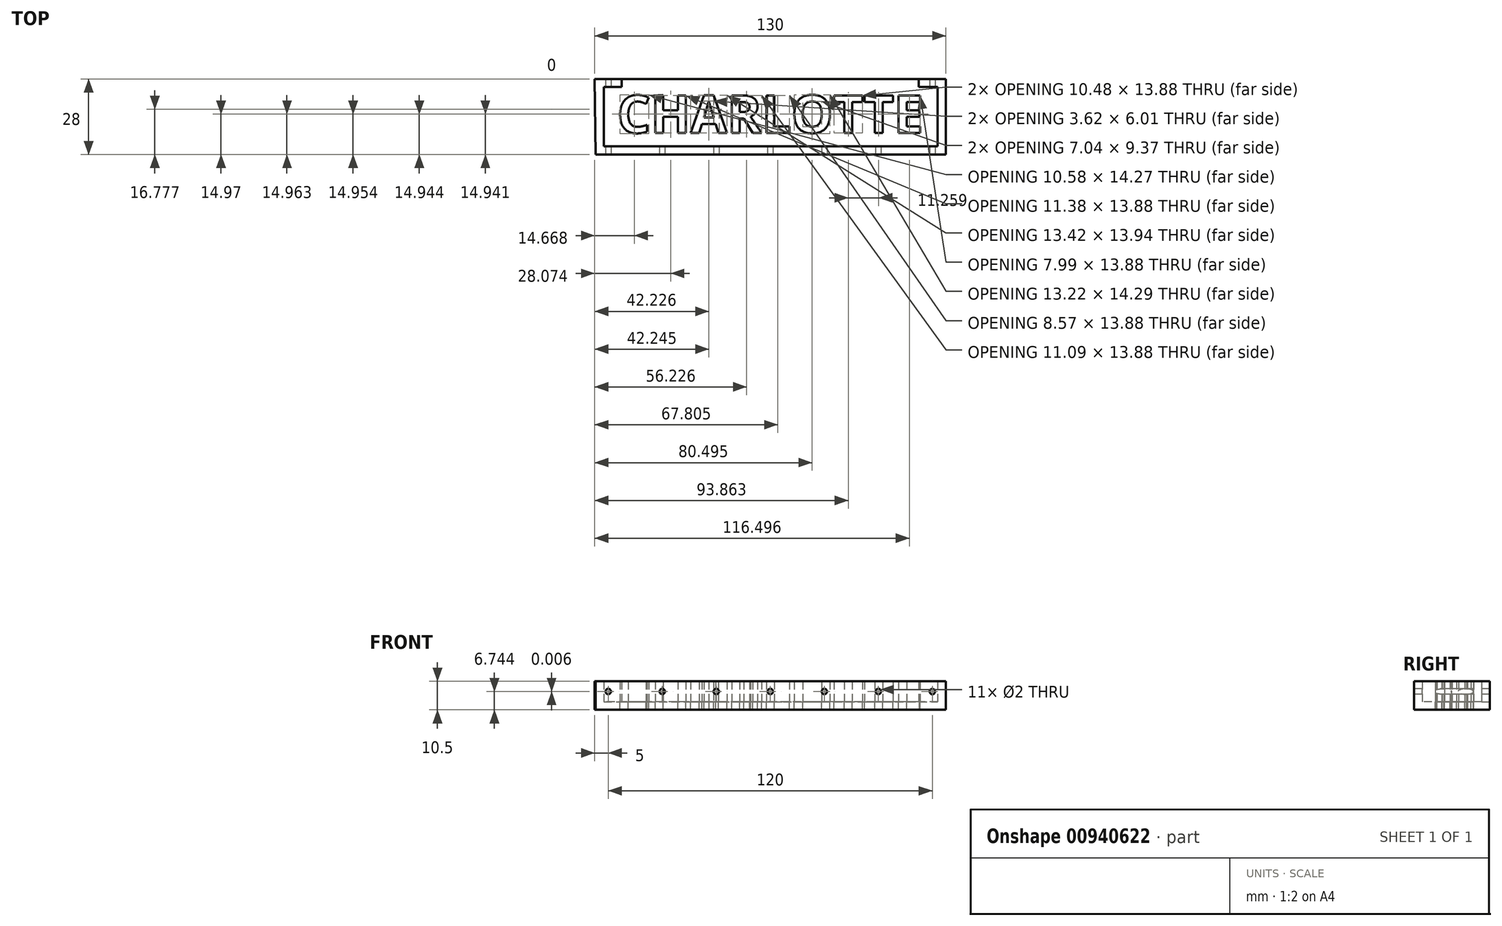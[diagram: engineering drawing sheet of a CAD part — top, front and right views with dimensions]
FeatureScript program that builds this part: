
annotation { "Feature Type Name" : "Feature", "Feature Type Description" : "" }
export const myFeature = defineFeature(function(context is Context, id is Id, definition is map)
    precondition{}
    {
        {
            var Q0;
            Q0=qCreatedBy(makeId("Top.planeOp"),FACE);
            var sketch = newSketch(context, id + "F0", { "sketchPlane" : qUnion([Q0])});
            skText(sketch, "E0", { "text": "CHARLOTTE", "fontName": "OpenSans-Bold.ttf"});
            skLineSegment(sketch, "E1", {"start": v(62, 11) * mm, "end": v(62, -11) * mm});
            skLineSegment(sketch, "E2", {"start": v(62, -11) * mm, "end": v(-61.65, -11) * mm});
            skLineSegment(sketch, "E3", {"start": v(-61.65, -11) * mm, "end": v(-61.65, 11) * mm});
            skLineSegment(sketch, "E4", {"start": v(-65, 14) * mm, "end": v(65, 14) * mm});
            skLineSegment(sketch, "E5", {"start": v(65, 14) * mm, "end": v(65, -14) * mm});
            skLineSegment(sketch, "E6", {"start": v(65, -14) * mm, "end": v(-64.65, -14) * mm});
            skLineSegment(sketch, "E7", {"start": v(-64.65, -14) * mm, "end": v(-65, 14) * mm});
            skPoint(sketch, "E8", {"position": v(0, 14) * mm});
            skPoint(sketch, "E9", {"position": v(-64.83, 0) * mm});
            skPoint(sketch, "E9.positionSnap0", {"position": v(-64.83, 0) * mm});
            skPoint(sketch, "E10", {"position": v(-56.75, 1) * mm});
            skPoint(sketch, "E11", {"position": v(-55, 14) * mm});
            skPoint(sketch, "E12", {"position": v(-55, 11) * mm});
            skPoint(sketch, "E13", {"position": v(55, 14) * mm});
            skPoint(sketch, "E14", {"position": v(55, 11) * mm});
            skLineSegment(sketch, "E15", {"start": v(-55, 11) * mm, "end": v(-55, 14) * mm});
            skLineSegment(sketch, "E16", {"start": v(55, 11) * mm, "end": v(55, 14) * mm});
            skLineSegment(sketch, "E17", {"start": v(-61.65, 11) * mm, "end": v(-55, 11) * mm});
            skLineSegment(sketch, "E18", {"start": v(55, 11) * mm, "end": v(62, 11) * mm});
            const initialGuessF0  = {"E0": [-0.05675, -0.006, 1, 0, 0.014]};
            skSetInitialGuess(sketch, initialGuessF0);
            skSolve(sketch);
        }
        {
            var Q0;
            Q0=makeQuery(id+"F0.imprint","IMPRINT",FACE,{"disambiguationData":[TD([[makeQuery(id+"F0.imprint","IMPRINT",EDGE,{"derivedFrom":sQuery(id+"F0.wireOp",EDGE,"E1")}),1.0]])]});
            var Q1;
            Q1=makeQuery(id+"F0.imprint","IMPRINT",FACE,{"disambiguationData":[TD([[makeQuery(id+"F0.imprint","IMPRINT",EDGE,{"derivedFrom":sQuery(id+"F0.wireOp",EDGE,"E0.sketch_text.stroke-15")}),-1.0]])]});
            var Q2;
            Q2=makeQuery(id+"F0.imprint","IMPRINT",FACE,{"disambiguationData":[TD([[makeQuery(id+"F0.imprint","IMPRINT",EDGE,{"derivedFrom":sQuery(id+"F0.wireOp",EDGE,"E0.sketch_text.stroke-64")}),-1.0]])]});
            var Q3;
            Q3=makeQuery(id+"F0.imprint","IMPRINT",FACE,{"disambiguationData":[TD([[makeQuery(id+"F0.imprint","IMPRINT",EDGE,{"derivedFrom":sQuery(id+"F0.wireOp",EDGE,"E0.sketch_text.stroke-58")}),-1.0]])]});
            var Q4;
            Q4=makeQuery(id+"F0.imprint","IMPRINT",FACE,{"disambiguationData":[TD([[makeQuery(id+"F0.imprint","IMPRINT",EDGE,{"derivedFrom":sQuery(id+"F0.wireOp",EDGE,"E0.sketch_text.stroke-39")}),-1.0]])]});
            var Q5;
            Q5=makeQuery(id+"F0.imprint","IMPRINT",FACE,{"disambiguationData":[TD([[makeQuery(id+"F0.imprint","IMPRINT",EDGE,{"derivedFrom":sQuery(id+"F0.wireOp",EDGE,"E0.sketch_text.stroke-27")}),-1.0]])]});
            var Q6;
            Q6=makeQuery(id+"F0.imprint","IMPRINT",FACE,{"disambiguationData":[TD([[makeQuery(id+"F0.imprint","IMPRINT",EDGE,{"derivedFrom":sQuery(id+"F0.wireOp",EDGE,"E0.sketch_text.stroke-78")}),-1.0]])]});
            var Q7;
            Q7=makeQuery(id+"F0.imprint","IMPRINT",FACE,{"disambiguationData":[TD([[makeQuery(id+"F0.imprint","IMPRINT",EDGE,{"derivedFrom":sQuery(id+"F0.wireOp",EDGE,"E0.sketch_text.stroke-86")}),-1.0]])]});
            var Q8;
            Q8=makeQuery(id+"F0.imprint","IMPRINT",FACE,{"disambiguationData":[TD([[makeQuery(id+"F0.imprint","IMPRINT",EDGE,{"derivedFrom":sQuery(id+"F0.wireOp",EDGE,"E0.sketch_text.stroke-94")}),-1.0]])]});
            var Q9;
            Q9=makeQuery(id+"F0.imprint","IMPRINT",FACE,{"disambiguationData":[TD([[makeQuery(id+"F0.imprint","IMPRINT",EDGE,{"derivedFrom":sQuery(id+"F0.wireOp",EDGE,"E0.sketch_text.stroke-0")}),-1.0]])]});
            extrude(context, id + "F1", {"entities" : qUnion([Q0, Q1, Q2, Q3, Q4, Q5, Q6, Q7, Q8, Q9]), "depth" : 7.5 * mm});
        }
        {
            var Q0;
            Q0=qSketchRegion(id+"F0",true);
            extrude(context, id + "F2", {"entities" : qUnion([Q0]), "operationType" : NewBodyOperationType.ADD, "depth" : -3 * mm});
        }
        {
            var Q0;
            {var subQ0=sQuery(id+"F0.wireOp",EDGE,"E6");Q0=makeQuery(id+"F2.boolean.opBoolean","MERGE",FACE,{"derivedFrom":[makeQuery(id+"F1.opExtrude","SWEPT_FACE",FACE,{"disambiguationData":[OSD([subQ0])]}),makeQuery(id+"F2.opExtrude","SWEPT_FACE",FACE,{"disambiguationData":[OSD([subQ0])]})]});}
            var sketch = newSketch(context, id + "F3", { "sketchPlane" : qUnion([Q0])});
            skPoint(sketch, "E19", {"position": v(-60, 3.75) * mm});
            skPoint(sketch, "E20", {"position": v(60, 3.74) * mm});
            skPoint(sketch, "E21", {"position": v(-40, 3.75) * mm});
            skPoint(sketch, "E22", {"position": v(-20, 3.75) * mm});
            skPoint(sketch, "E23", {"position": v(0, 3.75) * mm});
            skPoint(sketch, "E24", {"position": v(20, 3.75) * mm});
            skPoint(sketch, "E25", {"position": v(40, 3.75) * mm});
            skSolve(sketch);
        }
        {
            var Q0;
            Q0=sQuery(id+"F3.wireOp",VERTEX,"E19");
            var Q1;
            Q1=sQuery(id+"F3.wireOp",VERTEX,"E21");
            var Q2;
            Q2=sQuery(id+"F3.wireOp",VERTEX,"E22");
            var Q3;
            Q3=sQuery(id+"F3.wireOp",VERTEX,"E23");
            var Q4;
            Q4=sQuery(id+"F3.wireOp",VERTEX,"E24");
            var Q5;
            Q5=sQuery(id+"F3.wireOp",VERTEX,"E25");
            var Q6;
            Q6=sQuery(id+"F3.wireOp",VERTEX,"E20");
            var Q7;
            Q7=makeQuery(id+"F1.opExtrude","SWEPT_BODY",BODY,{"disambiguationData":[OSD([sQuery(id+"F0.wireOp",EDGE,"E1"),sQuery(id+"F0.wireOp",EDGE,"E2"),sQuery(id+"F0.wireOp",EDGE,"E3"),sQuery(id+"F0.wireOp",EDGE,"E4"),sQuery(id+"F0.wireOp",EDGE,"E5"),sQuery(id+"F0.wireOp",EDGE,"E6"),sQuery(id+"F0.wireOp",EDGE,"E7"),sQuery(id+"F0.wireOp",EDGE,"E15"),sQuery(id+"F0.wireOp",EDGE,"E16"),sQuery(id+"F0.wireOp",EDGE,"E17"),sQuery(id+"F0.wireOp",EDGE,"E18")])]});
            var Q8;
            Q8=makeQuery(id+"F1.opExtrude","SWEPT_BODY",BODY,{"disambiguationData":[OSD([sQuery(id+"F0.wireOp",EDGE,"E0.sketch_text.stroke-0"),sQuery(id+"F0.wireOp",EDGE,"E0.sketch_text.stroke-1"),sQuery(id+"F0.wireOp",EDGE,"E0.sketch_text.stroke-2"),sQuery(id+"F0.wireOp",EDGE,"E0.sketch_text.stroke-3"),sQuery(id+"F0.wireOp",EDGE,"E0.sketch_text.stroke-4"),sQuery(id+"F0.wireOp",EDGE,"E0.sketch_text.stroke-5"),sQuery(id+"F0.wireOp",EDGE,"E0.sketch_text.stroke-6"),sQuery(id+"F0.wireOp",EDGE,"E0.sketch_text.stroke-7"),sQuery(id+"F0.wireOp",EDGE,"E0.sketch_text.stroke-8"),sQuery(id+"F0.wireOp",EDGE,"E0.sketch_text.stroke-9"),sQuery(id+"F0.wireOp",EDGE,"E0.sketch_text.stroke-10"),sQuery(id+"F0.wireOp",EDGE,"E0.sketch_text.stroke-11"),sQuery(id+"F0.wireOp",EDGE,"E0.sketch_text.stroke-12"),sQuery(id+"F0.wireOp",EDGE,"E0.sketch_text.stroke-13"),sQuery(id+"F0.wireOp",EDGE,"E0.sketch_text.stroke-14")])]});
            var Q9;
            Q9=makeQuery(id+"F1.opExtrude","SWEPT_BODY",BODY,{"disambiguationData":[OSD([sQuery(id+"F0.wireOp",EDGE,"E0.sketch_text.stroke-27"),sQuery(id+"F0.wireOp",EDGE,"E0.sketch_text.stroke-28"),sQuery(id+"F0.wireOp",EDGE,"E0.sketch_text.stroke-29"),sQuery(id+"F0.wireOp",EDGE,"E0.sketch_text.stroke-30"),sQuery(id+"F0.wireOp",EDGE,"E0.sketch_text.stroke-31"),sQuery(id+"F0.wireOp",EDGE,"E0.sketch_text.stroke-32"),sQuery(id+"F0.wireOp",EDGE,"E0.sketch_text.stroke-33"),sQuery(id+"F0.wireOp",EDGE,"E0.sketch_text.stroke-34"),sQuery(id+"F0.wireOp",EDGE,"E0.sketch_text.stroke-35"),sQuery(id+"F0.wireOp",EDGE,"E0.sketch_text.stroke-36"),sQuery(id+"F0.wireOp",EDGE,"E0.sketch_text.stroke-37"),sQuery(id+"F0.wireOp",EDGE,"E0.sketch_text.stroke-38")])]});
            var Q10;
            Q10=makeQuery(id+"F1.opExtrude","SWEPT_BODY",BODY,{"disambiguationData":[OSD([sQuery(id+"F0.wireOp",EDGE,"E0.sketch_text.stroke-58"),sQuery(id+"F0.wireOp",EDGE,"E0.sketch_text.stroke-59"),sQuery(id+"F0.wireOp",EDGE,"E0.sketch_text.stroke-60"),sQuery(id+"F0.wireOp",EDGE,"E0.sketch_text.stroke-61"),sQuery(id+"F0.wireOp",EDGE,"E0.sketch_text.stroke-62"),sQuery(id+"F0.wireOp",EDGE,"E0.sketch_text.stroke-63")])]});
            var Q11;
            Q11=makeQuery(id+"F1.opExtrude","SWEPT_BODY",BODY,{"disambiguationData":[OSD([sQuery(id+"F0.wireOp",EDGE,"E0.sketch_text.stroke-78"),sQuery(id+"F0.wireOp",EDGE,"E0.sketch_text.stroke-79"),sQuery(id+"F0.wireOp",EDGE,"E0.sketch_text.stroke-80"),sQuery(id+"F0.wireOp",EDGE,"E0.sketch_text.stroke-81"),sQuery(id+"F0.wireOp",EDGE,"E0.sketch_text.stroke-82"),sQuery(id+"F0.wireOp",EDGE,"E0.sketch_text.stroke-83"),sQuery(id+"F0.wireOp",EDGE,"E0.sketch_text.stroke-84"),sQuery(id+"F0.wireOp",EDGE,"E0.sketch_text.stroke-85")])]});
            var Q12;
            Q12=makeQuery(id+"F1.opExtrude","SWEPT_BODY",BODY,{"disambiguationData":[OSD([sQuery(id+"F0.wireOp",EDGE,"E0.sketch_text.stroke-94"),sQuery(id+"F0.wireOp",EDGE,"E0.sketch_text.stroke-95"),sQuery(id+"F0.wireOp",EDGE,"E0.sketch_text.stroke-96"),sQuery(id+"F0.wireOp",EDGE,"E0.sketch_text.stroke-97"),sQuery(id+"F0.wireOp",EDGE,"E0.sketch_text.stroke-98"),sQuery(id+"F0.wireOp",EDGE,"E0.sketch_text.stroke-99"),sQuery(id+"F0.wireOp",EDGE,"E0.sketch_text.stroke-100"),sQuery(id+"F0.wireOp",EDGE,"E0.sketch_text.stroke-101"),sQuery(id+"F0.wireOp",EDGE,"E0.sketch_text.stroke-102"),sQuery(id+"F0.wireOp",EDGE,"E0.sketch_text.stroke-103"),sQuery(id+"F0.wireOp",EDGE,"E0.sketch_text.stroke-104"),sQuery(id+"F0.wireOp",EDGE,"E0.sketch_text.stroke-105")])]});
            hole(context, id + "F4", {"style" : HoleStyle.SIMPLE, "endStyle" : HoleEndStyle.THROUGH, "holeDiameter" : 2 * mm, "isTappedThrough" : true, "tappedDepth" : 12.7 * mm, "tapClearance" : 3, "locations" : qUnion([Q0, Q1, Q2, Q3, Q4, Q5, Q6]), "scope" : qUnion([Q7, Q8, Q9, Q10, Q11, Q12])});
        }
        {
            var Q0;
            Q0=makeQuery(id+"F1.opExtrude","CAP_FACE",FACE,{"disambiguationData":[OSD([sQuery(id+"F0.wireOp",EDGE,"E0.sketch_text.stroke-0"),sQuery(id+"F0.wireOp",EDGE,"E0.sketch_text.stroke-1"),sQuery(id+"F0.wireOp",EDGE,"E0.sketch_text.stroke-2"),sQuery(id+"F0.wireOp",EDGE,"E0.sketch_text.stroke-3"),sQuery(id+"F0.wireOp",EDGE,"E0.sketch_text.stroke-4"),sQuery(id+"F0.wireOp",EDGE,"E0.sketch_text.stroke-5"),sQuery(id+"F0.wireOp",EDGE,"E0.sketch_text.stroke-6"),sQuery(id+"F0.wireOp",EDGE,"E0.sketch_text.stroke-7"),sQuery(id+"F0.wireOp",EDGE,"E0.sketch_text.stroke-8"),sQuery(id+"F0.wireOp",EDGE,"E0.sketch_text.stroke-9"),sQuery(id+"F0.wireOp",EDGE,"E0.sketch_text.stroke-10"),sQuery(id+"F0.wireOp",EDGE,"E0.sketch_text.stroke-11"),sQuery(id+"F0.wireOp",EDGE,"E0.sketch_text.stroke-12"),sQuery(id+"F0.wireOp",EDGE,"E0.sketch_text.stroke-13"),sQuery(id+"F0.wireOp",EDGE,"E0.sketch_text.stroke-14")])],"isStart":true});
            var Q1;
            Q1=makeQuery(id+"F1.opExtrude","CAP_FACE",FACE,{"disambiguationData":[OSD([sQuery(id+"F0.wireOp",EDGE,"E0.sketch_text.stroke-15"),sQuery(id+"F0.wireOp",EDGE,"E0.sketch_text.stroke-16"),sQuery(id+"F0.wireOp",EDGE,"E0.sketch_text.stroke-17"),sQuery(id+"F0.wireOp",EDGE,"E0.sketch_text.stroke-18"),sQuery(id+"F0.wireOp",EDGE,"E0.sketch_text.stroke-19"),sQuery(id+"F0.wireOp",EDGE,"E0.sketch_text.stroke-20"),sQuery(id+"F0.wireOp",EDGE,"E0.sketch_text.stroke-21"),sQuery(id+"F0.wireOp",EDGE,"E0.sketch_text.stroke-22"),sQuery(id+"F0.wireOp",EDGE,"E0.sketch_text.stroke-23"),sQuery(id+"F0.wireOp",EDGE,"E0.sketch_text.stroke-24"),sQuery(id+"F0.wireOp",EDGE,"E0.sketch_text.stroke-25"),sQuery(id+"F0.wireOp",EDGE,"E0.sketch_text.stroke-26")])],"isStart":true});
            var Q2;
            Q2=makeQuery(id+"F1.opExtrude","CAP_FACE",FACE,{"disambiguationData":[OSD([sQuery(id+"F0.wireOp",EDGE,"E0.sketch_text.stroke-27"),sQuery(id+"F0.wireOp",EDGE,"E0.sketch_text.stroke-28"),sQuery(id+"F0.wireOp",EDGE,"E0.sketch_text.stroke-29"),sQuery(id+"F0.wireOp",EDGE,"E0.sketch_text.stroke-30"),sQuery(id+"F0.wireOp",EDGE,"E0.sketch_text.stroke-31"),sQuery(id+"F0.wireOp",EDGE,"E0.sketch_text.stroke-32"),sQuery(id+"F0.wireOp",EDGE,"E0.sketch_text.stroke-33"),sQuery(id+"F0.wireOp",EDGE,"E0.sketch_text.stroke-34"),sQuery(id+"F0.wireOp",EDGE,"E0.sketch_text.stroke-35"),sQuery(id+"F0.wireOp",EDGE,"E0.sketch_text.stroke-36"),sQuery(id+"F0.wireOp",EDGE,"E0.sketch_text.stroke-37"),sQuery(id+"F0.wireOp",EDGE,"E0.sketch_text.stroke-38")])],"isStart":true});
            var Q3;
            Q3=makeQuery(id+"F1.opExtrude","CAP_FACE",FACE,{"disambiguationData":[OSD([sQuery(id+"F0.wireOp",EDGE,"E0.sketch_text.stroke-39"),sQuery(id+"F0.wireOp",EDGE,"E0.sketch_text.stroke-40"),sQuery(id+"F0.wireOp",EDGE,"E0.sketch_text.stroke-41"),sQuery(id+"F0.wireOp",EDGE,"E0.sketch_text.stroke-42"),sQuery(id+"F0.wireOp",EDGE,"E0.sketch_text.stroke-43"),sQuery(id+"F0.wireOp",EDGE,"E0.sketch_text.stroke-44"),sQuery(id+"F0.wireOp",EDGE,"E0.sketch_text.stroke-45"),sQuery(id+"F0.wireOp",EDGE,"E0.sketch_text.stroke-46"),sQuery(id+"F0.wireOp",EDGE,"E0.sketch_text.stroke-47"),sQuery(id+"F0.wireOp",EDGE,"E0.sketch_text.stroke-48"),sQuery(id+"F0.wireOp",EDGE,"E0.sketch_text.stroke-49"),sQuery(id+"F0.wireOp",EDGE,"E0.sketch_text.stroke-50"),sQuery(id+"F0.wireOp",EDGE,"E0.sketch_text.stroke-51"),sQuery(id+"F0.wireOp",EDGE,"E0.sketch_text.stroke-52"),sQuery(id+"F0.wireOp",EDGE,"E0.sketch_text.stroke-53"),sQuery(id+"F0.wireOp",EDGE,"E0.sketch_text.stroke-54"),sQuery(id+"F0.wireOp",EDGE,"E0.sketch_text.stroke-55"),sQuery(id+"F0.wireOp",EDGE,"E0.sketch_text.stroke-56"),sQuery(id+"F0.wireOp",EDGE,"E0.sketch_text.stroke-57")])],"isStart":true});
            var Q4;
            Q4=makeQuery(id+"F1.opExtrude","CAP_FACE",FACE,{"disambiguationData":[OSD([sQuery(id+"F0.wireOp",EDGE,"E0.sketch_text.stroke-58"),sQuery(id+"F0.wireOp",EDGE,"E0.sketch_text.stroke-59"),sQuery(id+"F0.wireOp",EDGE,"E0.sketch_text.stroke-60"),sQuery(id+"F0.wireOp",EDGE,"E0.sketch_text.stroke-61"),sQuery(id+"F0.wireOp",EDGE,"E0.sketch_text.stroke-62"),sQuery(id+"F0.wireOp",EDGE,"E0.sketch_text.stroke-63")])],"isStart":true});
            var Q5;
            Q5=makeQuery(id+"F1.opExtrude","CAP_FACE",FACE,{"disambiguationData":[OSD([sQuery(id+"F0.wireOp",EDGE,"E0.sketch_text.stroke-64"),sQuery(id+"F0.wireOp",EDGE,"E0.sketch_text.stroke-65"),sQuery(id+"F0.wireOp",EDGE,"E0.sketch_text.stroke-66"),sQuery(id+"F0.wireOp",EDGE,"E0.sketch_text.stroke-67"),sQuery(id+"F0.wireOp",EDGE,"E0.sketch_text.stroke-68"),sQuery(id+"F0.wireOp",EDGE,"E0.sketch_text.stroke-69"),sQuery(id+"F0.wireOp",EDGE,"E0.sketch_text.stroke-70"),sQuery(id+"F0.wireOp",EDGE,"E0.sketch_text.stroke-71"),sQuery(id+"F0.wireOp",EDGE,"E0.sketch_text.stroke-72"),sQuery(id+"F0.wireOp",EDGE,"E0.sketch_text.stroke-73"),sQuery(id+"F0.wireOp",EDGE,"E0.sketch_text.stroke-74"),sQuery(id+"F0.wireOp",EDGE,"E0.sketch_text.stroke-75"),sQuery(id+"F0.wireOp",EDGE,"E0.sketch_text.stroke-76"),sQuery(id+"F0.wireOp",EDGE,"E0.sketch_text.stroke-77")])],"isStart":true});
            var Q6;
            Q6=makeQuery(id+"F1.opExtrude","CAP_FACE",FACE,{"disambiguationData":[OSD([sQuery(id+"F0.wireOp",EDGE,"E0.sketch_text.stroke-78"),sQuery(id+"F0.wireOp",EDGE,"E0.sketch_text.stroke-79"),sQuery(id+"F0.wireOp",EDGE,"E0.sketch_text.stroke-80"),sQuery(id+"F0.wireOp",EDGE,"E0.sketch_text.stroke-81"),sQuery(id+"F0.wireOp",EDGE,"E0.sketch_text.stroke-82"),sQuery(id+"F0.wireOp",EDGE,"E0.sketch_text.stroke-83"),sQuery(id+"F0.wireOp",EDGE,"E0.sketch_text.stroke-84"),sQuery(id+"F0.wireOp",EDGE,"E0.sketch_text.stroke-85")])],"isStart":true});
            var Q7;
            Q7=makeQuery(id+"F1.opExtrude","CAP_FACE",FACE,{"disambiguationData":[OSD([sQuery(id+"F0.wireOp",EDGE,"E0.sketch_text.stroke-86"),sQuery(id+"F0.wireOp",EDGE,"E0.sketch_text.stroke-87"),sQuery(id+"F0.wireOp",EDGE,"E0.sketch_text.stroke-88"),sQuery(id+"F0.wireOp",EDGE,"E0.sketch_text.stroke-89"),sQuery(id+"F0.wireOp",EDGE,"E0.sketch_text.stroke-90"),sQuery(id+"F0.wireOp",EDGE,"E0.sketch_text.stroke-91"),sQuery(id+"F0.wireOp",EDGE,"E0.sketch_text.stroke-92"),sQuery(id+"F0.wireOp",EDGE,"E0.sketch_text.stroke-93")])],"isStart":true});
            var Q8;
            Q8=makeQuery(id+"F1.opExtrude","CAP_FACE",FACE,{"disambiguationData":[OSD([sQuery(id+"F0.wireOp",EDGE,"E0.sketch_text.stroke-94"),sQuery(id+"F0.wireOp",EDGE,"E0.sketch_text.stroke-95"),sQuery(id+"F0.wireOp",EDGE,"E0.sketch_text.stroke-96"),sQuery(id+"F0.wireOp",EDGE,"E0.sketch_text.stroke-97"),sQuery(id+"F0.wireOp",EDGE,"E0.sketch_text.stroke-98"),sQuery(id+"F0.wireOp",EDGE,"E0.sketch_text.stroke-99"),sQuery(id+"F0.wireOp",EDGE,"E0.sketch_text.stroke-100"),sQuery(id+"F0.wireOp",EDGE,"E0.sketch_text.stroke-101"),sQuery(id+"F0.wireOp",EDGE,"E0.sketch_text.stroke-102"),sQuery(id+"F0.wireOp",EDGE,"E0.sketch_text.stroke-103"),sQuery(id+"F0.wireOp",EDGE,"E0.sketch_text.stroke-104"),sQuery(id+"F0.wireOp",EDGE,"E0.sketch_text.stroke-105")])],"isStart":true});
            extrude(context, id + "F5", {"entities" : qUnion([Q0, Q1, Q2, Q3, Q4, Q5, Q6, Q7, Q8]), "depth" : 3 * mm});
        }
    });
